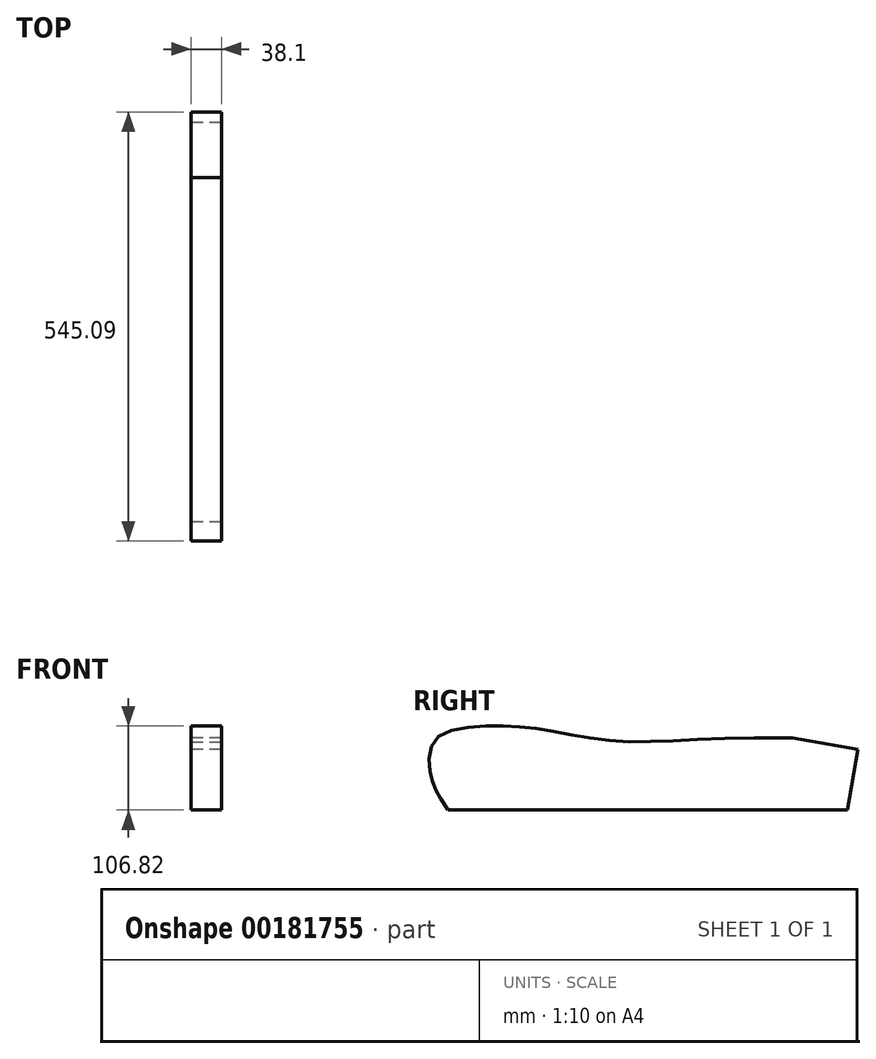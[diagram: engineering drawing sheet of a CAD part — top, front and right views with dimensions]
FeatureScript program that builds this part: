
annotation { "Feature Type Name" : "Feature", "Feature Type Description" : "" }
export const myFeature = defineFeature(function(context is Context, id is Id, definition is map)
    precondition{}
    {
        {
            var Q0;
            Q0=qCreatedBy(makeId("Right.planeOp"),FACE);
            var sketch = newSketch(context, id + "F0", { "sketchPlane" : qUnion([Q0])});
            skLineSegment(sketch, "E0.top", {"start": v(-77.84, -140.37) * mm, "end": v(429.6, -140.37) * mm});
            skFitSpline(sketch, "E1", {"points": [v(-77.84, -140.37) * mm, v(-94.1, -112.32) * mm, v(-101.52, -85.64) * mm, v(-91.94, -48.69) * mm, v(-29, -33.7) * mm, v(43.52, -38.18) * mm, v(132.84, -52.67) * mm, v(270.54, -49.55) * mm, v(446.34, -45.4) * mm], "startDerivative": vector(-320.46, 494.52) * mm, "endDerivative": vector(470.68, 75.63) * mm});
            skPoint(sketch, "E0.bottom.start.orphan", {"position": v(-133.84, 0) * mm});
            skLineSegment(sketch, "E2", {"start": v(443.13, -63.6) * mm, "end": v(429.6, -140.37) * mm});
            skLineSegment(sketch, "E3", {"start": v(359.94, -48.93) * mm, "end": v(311.63, -48.93) * mm});
            skLineSegment(sketch, "E4", {"start": v(359.94, -48.93) * mm, "end": v(443.13, -63.6) * mm});
            skSolve(sketch);
        }
        {
            var Q0;
            Q0 = qSketchRegion(id + "F0", true);
            extrude(context, id + "F1", {"entities" : qUnion([Q0]), "depth" : 38.1 * mm});
        }
    });
